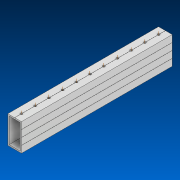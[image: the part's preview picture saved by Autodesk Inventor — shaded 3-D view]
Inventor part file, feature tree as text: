
AUTODESK INVENTOR PART (.ipt)
format: ipt  version: 2022.2 (Build 262287000, 287)  size: 449,536 bytes
history: native  units: in
note: dims shown in document units (in); Inventor stores cm internally (conversion verified against a paired STEP export)
features: other x12, extrude x1, pattern_linear x1, sketch x1
ambient origin geometry x8: Origin, YZ Plane, XZ Plane, XY Plane, X Axis, Y Axis, Z Axis, Center Point
bodies: Solid1 (feature_tree)
feature tree (15):
  extrude  "Extrusion1"  Depth=2.0in
  other  "Work Axis1"
  pattern_linear  "Rectangular Pattern1"  Spacing1=48.0in  [1 undecoded]
  sketch  "Sketch1"  dims[d0=1.0in d1=2.0in d2=48.0in d3=0.0in d4=4.3307in d6=1.0in]
  other  "Work Axis2"
  other  "Work Axis3"
  other  "Work Axis4"
  other  "Work Axis5"
  other  "Work Axis6"
  other  "Work Axis7"
  other  "Work Axis8"
  other  "Work Axis9"
  other  "Work Axis10"
  other  "Work Axis60"
  other  "Cut-Extrude2"
note: 1 required parameter value undecoded (feature->parameter linkage not recoverable at this tier; creation-order binding heuristic only, values carry confidence <= 0.55)
